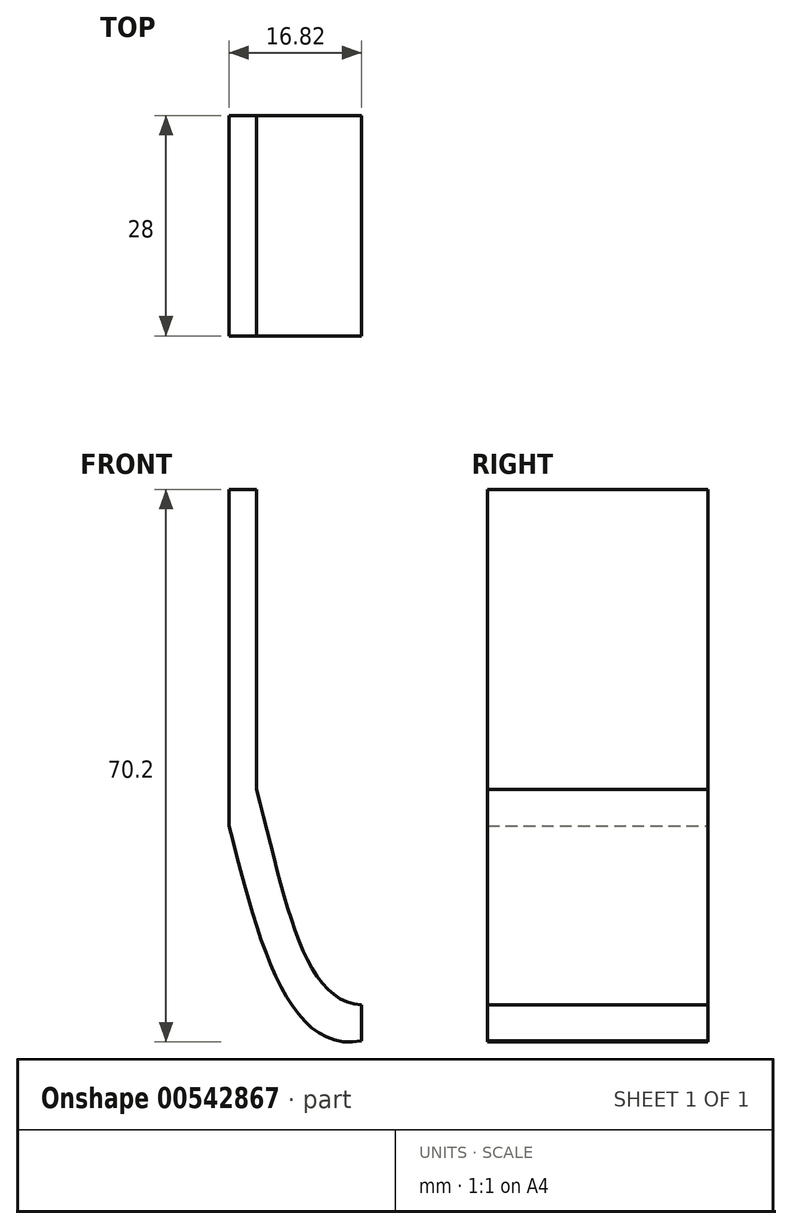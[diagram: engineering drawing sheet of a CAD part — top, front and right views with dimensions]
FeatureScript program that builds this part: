
annotation { "Feature Type Name" : "Feature", "Feature Type Description" : "" }
export const myFeature = defineFeature(function(context is Context, id is Id, definition is map)
    precondition{}
    {
        {
            var Q0;
            Q0=qCreatedBy(makeId("Front.planeOp"),FACE);
            var sketch = newSketch(context, id + "F0", { "sketchPlane" : qUnion([Q0])});
            skLineSegment(sketch, "E0.bottom", {"start": v(-8.03, 34.61) * mm, "end": v(-4.53, 34.61) * mm});
            skLineSegment(sketch, "E0.left", {"start": v(-8.03, 34.61) * mm, "end": v(-8.03, -8.13) * mm});
            skLineSegment(sketch, "E0.right", {"start": v(-4.53, 34.61) * mm, "end": v(-4.53, -3.48) * mm});
            skLineSegment(sketch, "E1.left", {"start": v(-8.03, -3.48) * mm, "end": v(-8.03, -8.13) * mm});
            skLineSegment(sketch, "E1.right", {"start": v(8.79, -30.87) * mm, "end": v(8.79, -37.03) * mm});
            skFitSpline(sketch, "E2", {"points": [v(-8.03, -8.13) * mm, v(8.79, -35.45) * mm, v(34.08, -12.64) * mm, v(33.8, -12.36) * mm, v(34.63, -11.95) * mm], "startDerivative": vector(25.5, -100.65) * mm, "endDerivative": vector(17.5, 6.8) * mm});
            skFitSpline(sketch, "E3", {"points": [v(-4.53, -3.48) * mm, v(8.79, -30.87) * mm, v(21.03, -25.27) * mm, v(20.78, -25.27) * mm, v(21.1, -25.02) * mm, v(21.2, -25.27) * mm], "startDerivative": vector(20.93, -79.25) * mm, "endDerivative": vector(-0.11, -7.93) * mm});
            skSolve(sketch);
        }
        {
            var Q0;
            Q0=makeQuery(id+"F0.imprint","IMPRINT",FACE,{"disambiguationData":[TD([[makeQuery(id+"F0.imprint","IMPRINT",EDGE,{"derivedFrom":sQuery(id+"F0.wireOp",EDGE,"E0.bottom")}),-1.0]])]});
            extrude(context, id + "F1", {"entities" : qUnion([Q0]), "depth" : 28 * mm, "offsetDistance" : 25 * mm});
        }
    });
